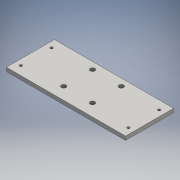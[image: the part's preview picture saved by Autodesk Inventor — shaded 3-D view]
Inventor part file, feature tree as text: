
AUTODESK INVENTOR PART (.ipt)
format: ipt  version: 2016 (Build 200138000, 138)  size: 123,904 bytes
history: native  units: mm
features: sketch x3, hole x2, extrude x1
ambient origin geometry x8: Origin, YZ Plane, XZ Plane, XY Plane, X Axis, Y Axis, Z Axis, Center Point
bodies: Solid1 (feature_tree)
feature tree (6):
  extrude  "Extrusion1"  Depth=310.0mm
  hole  "Hole1"  [1 undecoded]
  hole  "Hole2"  [1 undecoded]
  sketch  "Sketch1"  dims[d0=125.0mm d1=310.0mm]
  sketch  "Sketch2"  dims[d2=155.0mm d3=62.5mm]
  sketch  "Sketch3"  dims[d4=10.0mm d5=0.0mm d6=75.0mm d7=18.475mm d8=75.0mm d9=6.6mm d10=6.0mm d11=12.0mm d12=7.0mm d13=14.3117mm d14=8.0mm d15=20.594885mm d16=80.0mm d17=40.0mm d18=280.0mm d19=140.0mm d20=6.6mm d21=6.0mm d22=18.0mm d23=7.0mm d24=14.3117mm d25=8.0mm d26=20.594885mm d27=37.5mm]
note: 2 required parameter values undecoded (feature->parameter linkage not recoverable at this tier; creation-order binding heuristic only, values carry confidence <= 0.55)
